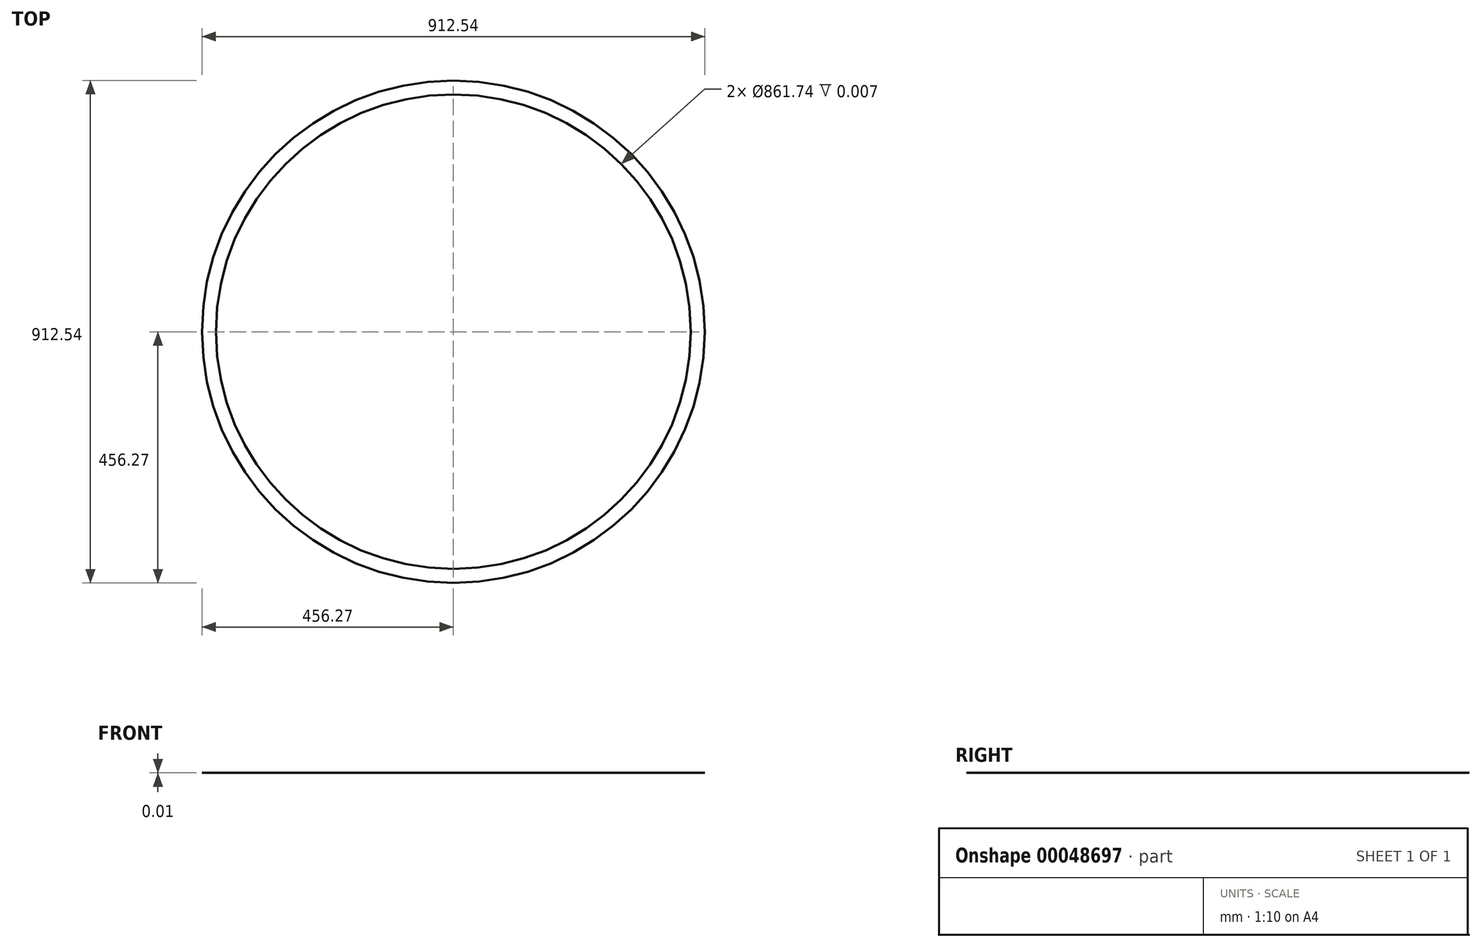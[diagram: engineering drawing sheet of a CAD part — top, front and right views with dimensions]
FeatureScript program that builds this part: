
annotation { "Feature Type Name" : "Feature", "Feature Type Description" : "" }
export const myFeature = defineFeature(function(context is Context, id is Id, definition is map)
    precondition{}
    {
        {
            var Q0;
            Q0=qCreatedBy(makeId("Top.planeOp"),FACE);
            var sketch = newSketch(context, id + "F0", { "sketchPlane" : qUnion([Q0])});
            skCircle(sketch, "E0", {"center": v(0, 0) * mm, "radius": 456.27 * mm});
            skCircle(sketch, "E1", {"center": v(0, 0) * mm, "radius": 430.87 * mm});
            skSolve(sketch);
        }
        {
            var Q0;
            Q0=makeQuery(id+"F0.imprint","IMPRINT",FACE,{"disambiguationData":[TD([[makeQuery(id+"F0.imprint","IMPRINT",EDGE,{"derivedFrom":sQuery(id+"F0.wireOp",EDGE,"E0")}),1.0]])]});
            extrude(context, id + "F1", {"entities" : qUnion([Q0]), "depth" : 3 / 457.2 * mm});
        }
        {
            var Q0;
            Q0=makeQuery(id+"F0.imprint","IMPRINT",FACE,{"disambiguationData":[TD([[makeQuery(id+"F0.imprint","IMPRINT",EDGE,{"derivedFrom":sQuery(id+"F0.wireOp",EDGE,"E0")}),1.0]])]});
            extrude(context, id + "F2", {"entities" : qUnion([Q0]), "depth" : 3 / 457.2 * mm});
        }
    });
